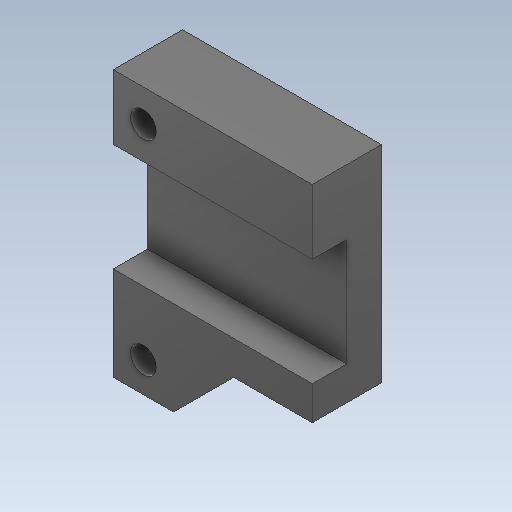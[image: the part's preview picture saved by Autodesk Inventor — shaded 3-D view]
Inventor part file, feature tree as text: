
AUTODESK INVENTOR PART (.ipt)
format: ipt  version: 2020 (Build 240168000, 168)  size: 687,104 bytes
history: native  units: mm
features: extrude x31, sketch x29, projected_geometry x21, reference x8, other x5, chamfer x4, plane x1, hole x1
ambient origin geometry x8: Origin, YZ Plane, XZ Plane, XY Plane, X Axis, Y Axis, Z Axis, Center Point
bodies: Solid1 (feature_tree)
feature tree (100):
  extrude  "Extrusion1"  Depth=45.0mm
  plane  "Work Plane1"
  extrude  "Extrusion2"  Depth=18.0mm
  extrude  "Extrusion3"  Depth=2.0mm TaperAngle=0.0deg
  extrude  "Extrusion4"  TaperAngle=0.0deg  [1 undecoded]
  extrude  "Extrusion5"  Depth=50.1mm TaperAngle=0.0deg
  sketch  "Sketch6"  dims[d14=7.199887mm d15=3.599976mm]
  extrude  "Extrusion6"  Depth=3.599976mm
  extrude  "Extrusion7"  Depth=0.15mm
  extrude  "Extrusion8"  Depth=0.15mm
  extrude  "Extrusion10"  Depth=15.9mm TaperAngle=0.0deg
  extrude  "Extrusion11"  Depth=23.15mm
  extrude  "Extrusion12"  Depth=3.925mm
  extrude  "Extrusion13"  Depth=5.15mm
  sketch  "Sketch14"  dims[d29=2.525mm d30=5.15mm]
  extrude  "Extrusion14"  Depth=12.55mm
  extrude  "Extrusion15"  Depth=2.75mm TaperAngle=0.0deg
  hole  "Hole1"  [1 undecoded]
  extrude  "Extrusion16"  Depth=3.925mm
  extrude  "Extrusion18"  Depth=23.15mm
  extrude  "Extrusion20"  Depth=10.0mm
  extrude  "Extrusion21"  Depth=0.0mm
  extrude  "Extrusion22"  TaperAngle=0.0deg  [1 undecoded]
  chamfer  "Chamfer1"  Distance=12.55mm
  extrude  "Extrusion23"  Depth=10.0mm
  extrude  "Extrusion24"  Depth=0.5mm
  chamfer  "Chamfer2"  Distance=17.225mm
  extrude  "Extrusion25"  Depth=4.0mm TaperAngle=0.0deg
  extrude  "Extrusion26"  Depth=0.5mm
  extrude  "Extrusion28"  Depth=10.925mm
  extrude  "Extrusion31"  Depth=0.5mm TaperAngle=0.0deg
  extrude  "Extrusion32"  Depth=0.5mm
  extrude  "Extrusion35"  Depth=0.5mm TaperAngle=0.0deg
  extrude  "Extrusion36"  Depth=0.5mm
  extrude  "Extrusion37"  Depth=0.5mm
  extrude  "Extrusion38"  Depth=0.5mm
  chamfer  "Chamfer4"  Distance=53.1mm
  chamfer  "Chamfer6"  Distance=53.1mm
  extrude  "Extrusion39"  Depth=0.5mm
  sketch  "Sketch1"  dims[d0=18.0mm d1=45.0mm]
  reference  "Reference1"
  sketch  "Sketch2"  dims[d2=45.0mm d3=18.0mm]
  reference  "Reference2"
  sketch  "Sketch3"  dims[d4=18.0mm d5=51.1mm d6=2.0mm d7=0.0mm d8=0.0mm]
  reference  "Reference3"
  reference  "Reference4"
  reference  "Reference5"
  reference  "Reference6"
  reference  "Reference7"
  reference  "Reference8"
  sketch  "Sketch4"  dims[d9=37.3mm d10=0.0mm]
  sketch  "Sketch5"  dims[d11=35.0mm d12=50.1mm d13=0.0mm]
  sketch  "Sketch8"  dims[d16=0.15mm d17=0.15mm]
  sketch  "Sketch10"  dims[d18=0.15mm d19=0.15mm]
  sketch  "Sketch11"  dims[d20=5.4mm d21=0.0mm d22=15.9mm d23=0.0mm]
  sketch  "Sketch12"  dims[d24=6.5mm d25=0.0mm d26=23.15mm]
  sketch  "Sketch13"  dims[d27=12.55mm d28=3.925mm]
  sketch  "Sketch15"  dims[d31=5.15mm d32=12.55mm]
  sketch  "Sketch17"  dims[d33=40.75mm d34=0.0mm d35=2.75mm d36=0.0mm]
  sketch  "Sketch19"  dims[d43=11.85mm d44=23.15mm]
  projected_geometry  "Projected Loop1"
  sketch  "Sketch21"  dims[d45=3.925mm d46=2.525mm]
  projected_geometry  "Projected Loop3"
  sketch  "Sketch22"  dims[d47=12.55mm d48=23.15mm]
  sketch  "Sketch23"  dims[d49=10.05mm d50=0.0mm d54=10.0mm]
  projected_geometry  "Projected Loop4"
  projected_geometry  "Projected Loop5"
  projected_geometry  "Projected Loop6"
  projected_geometry  "Projected Loop7"
  sketch  "Sketch24"  dims[d55=0.0mm d56=0.0mm]
  projected_geometry  "Projected Loop8"
  sketch  "Sketch25"  dims[d57=19.0mm d58=0.0mm]
  projected_geometry  "Projected Loop9"
  projected_geometry  "Projected Loop10"
  projected_geometry  "Projected Loop11"
  projected_geometry  "Projected Loop12"
  sketch  "Sketch26"  dims[d59=8.8mm]
  projected_geometry  "Projected Loop13"
  sketch  "Sketch27"  dims[d60=5.925mm]
  projected_geometry  "Projected Loop14"
  sketch  "Sketch29"  dims[d61=2.525mm]
  projected_geometry  "Projected Loop16"
  sketch  "Sketch32"  dims[d62=23.15mm]
  projected_geometry  "Projected Loop19"
  sketch  "Sketch33"  dims[d63=15.075mm]
  projected_geometry  "Projected Loop20"
  sketch  "Sketch36"  dims[d64=23.15mm]
  projected_geometry  "Projected Loop23"
  projected_geometry  "Projected Loop24"
  projected_geometry  "Projected Loop25"
  sketch  "Sketch38"  dims[d65=6.05mm]
  projected_geometry  "Projected Loop26"
  sketch  "Sketch39"  dims[d66=23.15mm d67=12.55mm d68=0.0mm]
  projected_geometry  "Projected Loop27"
  sketch  "Sketch40"  dims[d72=8.8mm d73=10.0mm d74=10.2mm d75=17.225mm d76=4.0mm d77=0.0mm d78=3.85mm d79=10.925mm d80=5.0mm d81=0.0mm d82=0.765mm d83=2.7mm d84=0.0mm d85=18.0mm d86=5.0mm d87=5.0mm d88=53.1mm d89=0.0mm d90=53.1mm d91=0.0mm d92=3.0mm d93=6.0mm d94=4.0mm d95=2.0mm d96=90.0deg d97=40.0mm d98=0.0mm d99=3.1mm d100=2.4mm d101=0.0mm d105=3.1mm d106=2.4mm d107=0.0mm d112=8.0mm d113=24.0mm d114=3.0mm d115=26.0mm d116=3.0mm d117=4.0mm d118=4.0mm d119=12.0mm d120=10.0mm d121=0.0mm d122=3.1mm d123=3.1mm d124=2.4mm d125=0.0mm d126=37.142391mm d127=15.292019mm d128=67.65mm d129=0.0mm d130=3.0mm d131=2.0mm d132=45.0deg d133=20.0mm d134=18.0mm d135=4.5mm d136=6.0mm d137=6.0mm d138=1.5mm d139=1.5mm d140=1.5mm d141=27.781995mm d142=9.376677mm d143=25.5mm d144=3.376677mm d145=25.5mm d146=2.623323mm d147=25.5mm d148=90.0deg d149=25.571384mm d150=25.571384mm d151=0.023277mm d152=2.273277mm d153=6.349941mm d154=0.020391mm d155=0.026321mm d156=25.5mm d157=9.0mm d158=25.5mm d159=6.75mm d160=30.0mm d161=6.75mm d162=25.5mm d163=5.25mm d164=30.0mm d165=5.25mm d166=25.5mm d167=0.75mm d168=30.0mm d169=0.75mm d170=25.5mm d171=0.75mm d172=30.0mm d173=0.75mm d174=25.5mm d175=5.25mm d176=30.0mm d177=5.25mm d178=25.5mm d179=6.75mm d180=30.0mm d181=6.75mm d182=34.392739mm d183=25.5mm d184=9.0mm d185=34.394624mm d186=50.0mm d187=18.0mm d188=2.0mm d189=0.0mm d190=1.5mm d191=1.5mm d192=4.5mm d193=10.0mm d194=10.0mm d195=6.0mm d196=0.0mm d197=2.0mm d198=2.0mm d199=45.0deg d200=7.0mm d201=7.0mm d202=0.0mm d203=6.0mm d204=0.0mm d211=5.0mm d212=0.0mm d225=7.0mm d226=3.0mm d227=19.5mm d228=0.0mm d229=6.1mm d230=2.0mm d231=0.0mm d238=68.25mm d239=0.0mm d240=5.6mm d241=5.6mm d242=2.0mm d243=0.0mm d244=7.525mm d245=5.6mm d246=3.5mm d247=2.5mm d248=0.0mm d249=3.0mm d250=2.0mm d251=0.0mm d252=7.0mm d253=2.0mm d254=45.0deg d258=2.0mm d259=2.0mm d260=45.0deg d261=10.1mm d262=10.0mm d263=0.0mm d108=0.5mm d109=0.872665mm]
  parser-record x1  (decoder bookkeeping rows leaked as tree rows — omitted from the tree; the rows remain in map.json)
  other  "Demo2.0004.iam"
  other  "Bearing:2"
  other  "Rolling bearing GB/T 7218-1995 Type FSN 70000-Z F 623-Z:1"
  other  "servo horn 1:1"
note: 3 required parameter values undecoded (feature->parameter linkage not recoverable at this tier; creation-order binding heuristic only, values carry confidence <= 0.55)
note: 1 file-system path scrubbed to <path> (originals preserved in map.json)
